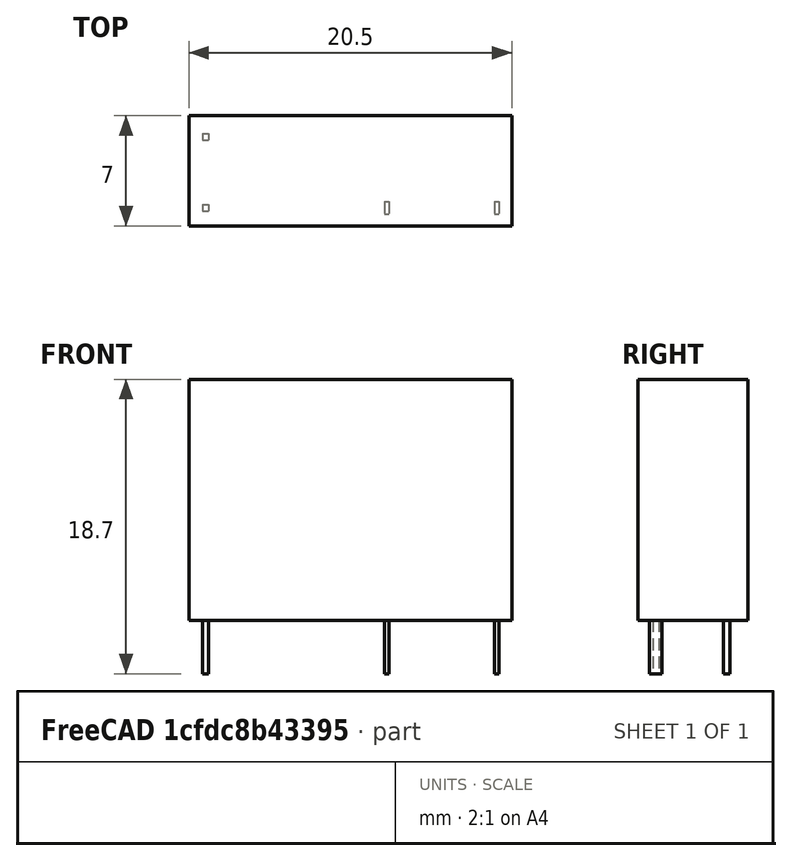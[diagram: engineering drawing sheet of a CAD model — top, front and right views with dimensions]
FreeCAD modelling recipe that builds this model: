
FCSTD DOCUMENT  (FreeCAD 0.17R13528 (Git))
Label: Relay-HF46F
License: All rights reserved
LicenseURL: http://en.wikipedia.org/wiki/All_rights_reserved
objects: Part::Box×4, Part::Feature×2, App::DocumentObjectGroup×1
note: 6 computed .brp shape members not serialized (recipe doc carries the construction recipe); baked Part::Feature solids carry a one-line shape summary decoded from their .brp

FEATURE [Part::Box] Box001  label="Coil_A"
  AttacherType = Attacher::AttachEngine3D
  Height = 3.4
  Length = 0.4
  Placement = pos=(0.85,1.35,0) rot=(1,0,0;3.14159rad)
  Width = 0.4
FEATURE [Part::Box] Box002  label="Coil_B"
  AttacherType = Attacher::AttachEngine3D
  Height = 3.4
  Length = 0.4
  Placement = pos=(0.85,5.85,0) rot=(1,0,0;3.14159rad)
  Width = 0.4
FEATURE [Part::Box] Box003  label="Output_A"
  AttacherType = Attacher::AttachEngine3D
  Height = 3.4
  Length = 0.3
  Placement = pos=(12.4,1.55,0) rot=(1,0,0;3.14159rad)
  Width = 0.8
FEATURE [Part::Box] Box004  label="Output_B"
  AttacherType = Attacher::AttachEngine3D
  Height = 3.4
  Length = 0.3
  Placement = pos=(19.4,1.55,0) rot=(1,0,0;3.14159rad)
  Width = 0.8
FEATURE [Part::Feature] Shape  label="Cube"
  shape: bbox 20.5 x 7 x 15.3 mm, 6 faces (baked)
FEATURE [App::DocumentObjectGroup] Group  label="Body"
  Group = -> [Shape,Box001,Box002,Box003,Box004]
FEATURE [Part::Feature] Shape001  label="Compound"
  shape: bbox 20.5 x 7 x 18.7 mm, 30 faces, 5 solids (baked)
